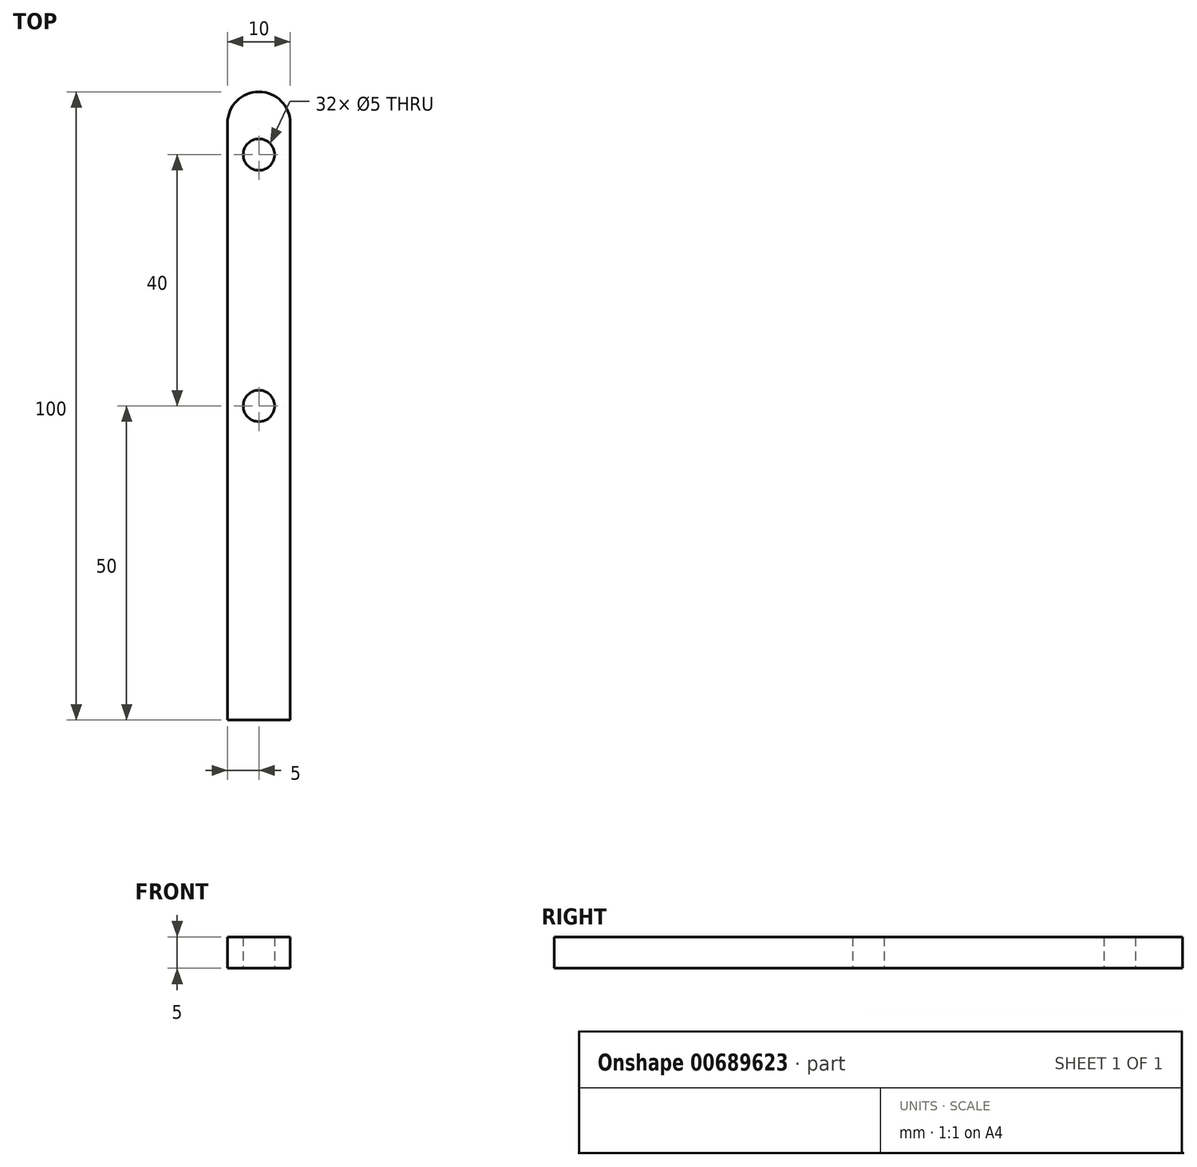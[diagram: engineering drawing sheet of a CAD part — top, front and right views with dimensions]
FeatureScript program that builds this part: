
annotation { "Feature Type Name" : "Feature", "Feature Type Description" : "" }
export const myFeature = defineFeature(function(context is Context, id is Id, definition is map)
    precondition{}
    {
        {
            var Q0;
            Q0=qCreatedBy(makeId("Top.planeOp"),FACE);
            var sketch = newSketch(context, id + "F0", { "sketchPlane" : qUnion([Q0])});
            skLineSegment(sketch, "E0", {"start": v(0, 0) * mm, "end": v(0, 100) * mm});
            skLineSegment(sketch, "E1", {"start": v(0, 100) * mm, "end": v(10, 100) * mm});
            skLineSegment(sketch, "E2", {"start": v(10, 100) * mm, "end": v(10, 0) * mm});
            skLineSegment(sketch, "E3", {"start": v(10, 0) * mm, "end": v(0, 0) * mm});
            skLineSegment(sketch, "E4", {"start": v(0, 0) * mm, "end": v(0, 50) * mm});
            skCircle(sketch, "E5", {"center": v(5, 50) * mm, "radius": 2.5 * mm});
            skCircle(sketch, "E6", {"center": v(5, 90) * mm, "radius": 2.5 * mm});
            skSolve(sketch);
        }
        {
            var Q0;
            Q0=makeQuery(id+"F0.imprint","IMPRINT",FACE,{"disambiguationData":[TD([[makeQuery(id+"F0.imprint","IMPRINT",EDGE,{"derivedFrom":sQuery(id+"F0.wireOp",EDGE,"E0")}),-1.0]])]});
            extrude(context, id + "F1", {"entities" : qUnion([Q0]), "depth" : 5 * mm, "offsetDistance" : 25 * mm});
        }
        {
            var Q0;
            Q0=makeQuery(id+"F1.opExtrude","SWEPT_EDGE",EDGE,{"disambiguationData":[OSD([sQuery(id+"F0.wireOp",EDGE,"E0"),sQuery(id+"F0.wireOp",EDGE,"E1")])]});
            var Q1;
            Q1=makeQuery(id+"F1.opExtrude","SWEPT_EDGE",EDGE,{"disambiguationData":[OSD([sQuery(id+"F0.wireOp",EDGE,"E1"),sQuery(id+"F0.wireOp",EDGE,"E2")])]});
            fillet(context, id + "F2", {"entities" : qUnion([Q0, Q1]), "radius" : 5 * mm, "tangentPropagation" : true, "allowEdgeOverflow" : false});
        }
    });
